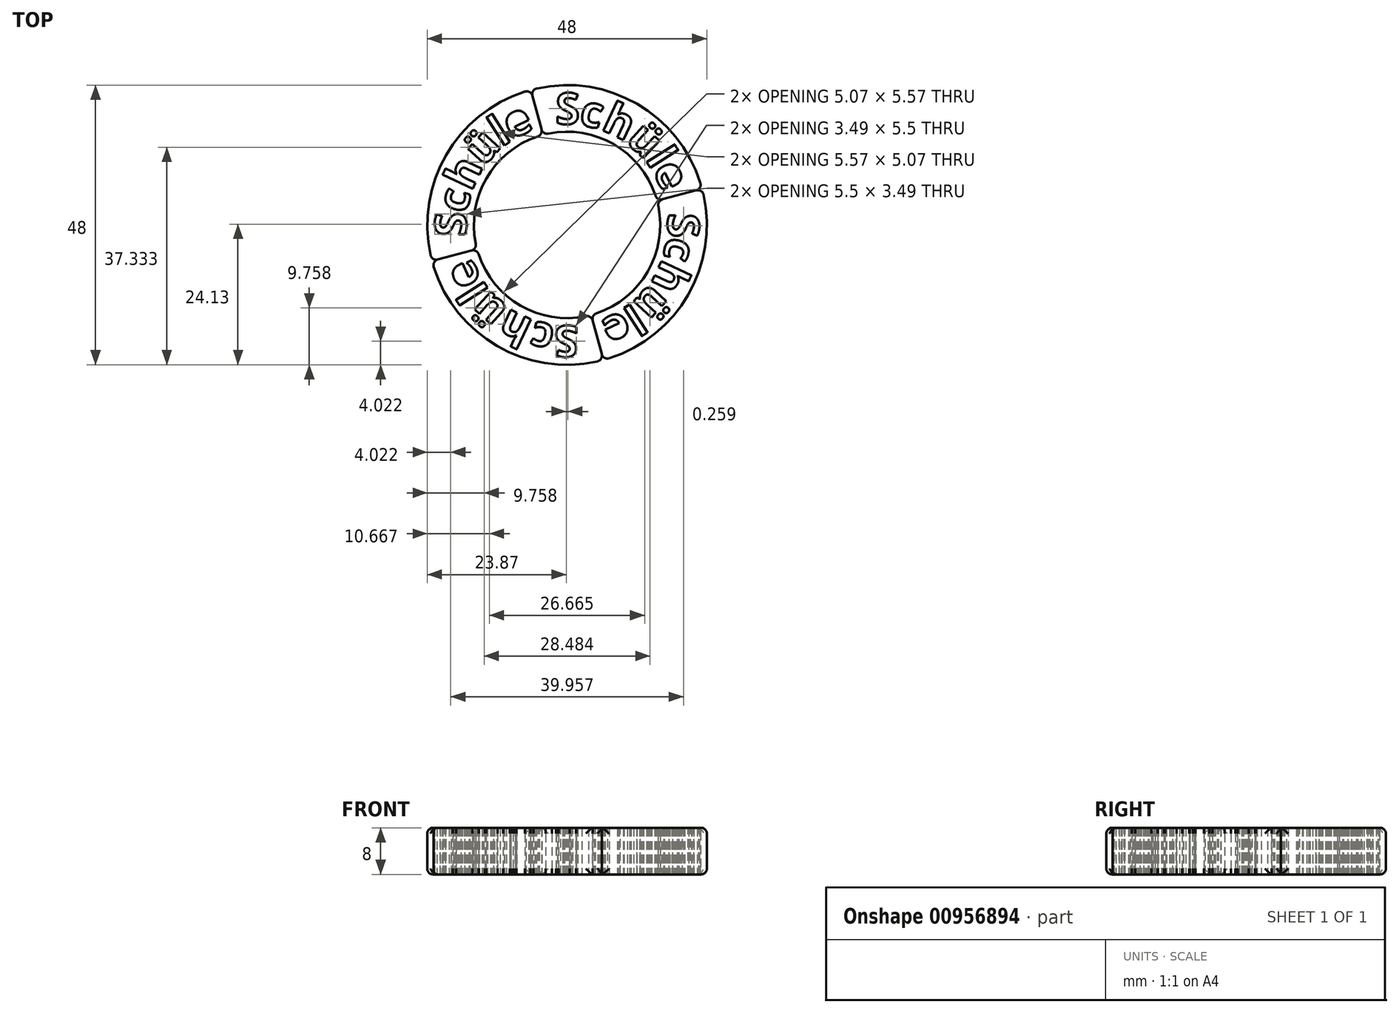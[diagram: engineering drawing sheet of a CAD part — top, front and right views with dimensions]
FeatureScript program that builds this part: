
annotation { "Feature Type Name" : "Feature", "Feature Type Description" : "" }
export const myFeature = defineFeature(function(context is Context, id is Id, definition is map)
    precondition{}
    {
        {
            var Q0;
            Q0=qCreatedBy(makeId("Top.planeOp"),FACE);
            var sketch = newSketch(context, id + "F0", { "sketchPlane" : qUnion([Q0])});
            skArc(sketch, "E0", {"start": v(23.18, 6.21) * mm, "mid": v(12, 20.78) * mm, "end": v(-6.21, 23.18) * mm});
            skArc(sketch, "E1", {"start": v(15.45, 4.14) * mm, "mid": v(8, 13.86) * mm, "end": v(-4.14, 15.45) * mm});
            skText(sketch, "E2", { "text": "c", "fontName": "OpenSans-Bold.ttf"});
            skText(sketch, "E3", { "text": "S", "fontName": "OpenSans-Bold.ttf"});
            skText(sketch, "E4", { "text": "h", "fontName": "OpenSans-Bold.ttf"});
            skText(sketch, "E5", { "text": "ü", "fontName": "OpenSans-Bold.ttf"});
            skText(sketch, "E6", { "text": "l", "fontName": "OpenSans-Bold.ttf"});
            skText(sketch, "E7", { "text": "e", "fontName": "OpenSans-Bold.ttf"});
            skLineSegment(sketch, "E8", {"start": v(15.45, 4.14) * mm, "end": v(23.18, 6.21) * mm});
            skLineSegment(sketch, "E9", {"start": v(-4.14, 15.45) * mm, "end": v(-6.21, 23.18) * mm});
            skLineSegment(sketch, "E10", {"start": v(0, 0) * mm, "end": v(15.45, 4.14) * mm});
            skPoint(sketch, "E11.start.orphan", {"position": v(0, 24) * mm});
            skLineSegment(sketch, "E12", {"start": v(-4.14, 15.45) * mm, "end": v(0, 0) * mm});
            skCircle(sketch, "E13", {"center": v(0, 0) * mm, "radius": 15.95 * mm});
            const initialGuessF0  = {"E2": [0.00188, 0.01736, 0.97037, -0.2416, 0.00533], "E3": [-0.00196, 0.0173, 1, 0, 0.0054], "E4": [0.0057, 0.01644, 0.90447, -0.42653, 0.0054], "E5": [0.0099, 0.01439, 0.73728, -0.6756, 0.0054], "E6": [0.01335, 0.01124, 0.53804, -0.84292, 0.0054], "E7": [0.01463, 0.00952, 0.43051, -0.90259, 0.0054]};
            skSetInitialGuess(sketch, initialGuessF0);
            skSolve(sketch);
        }
        {
            var Q0;
            Q0=makeQuery(id+"F0.imprint","IMPRINT",FACE,{"disambiguationData":[TD([[makeQuery(id+"F0.imprint","IMPRINT",EDGE,{"derivedFrom":sQuery(id+"F0.wireOp",EDGE,"E0")}),1.0]])]});
            var Q1;
            Q1=makeQuery(id+"F0.imprint","IMPRINT",FACE,{"disambiguationData":[TD([[makeQuery(id+"F0.imprint","IMPRINT",EDGE,{"derivedFrom":sQuery(id+"F0.wireOp",EDGE,"E2.sketch_text.stroke-0")}),1.0]])]});
            var Q2;
            {var subQ0=sQuery(id+"F0.wireOp",EDGE,"E10");Q2=makeQuery(id+"F0.imprint","IMPRINT",FACE,{"disambiguationData":[TD([[makeQuery(id+"F0.imprint","IMPRINT",EDGE,{"derivedFrom":subQ0}),1.0]])]});}
            extrude(context, id + "F1", {"entities" : qUnion([Q0, Q1, Q2]), "depth" : 8 * mm, "offsetDistance" : 25 * mm});
        }
        {
            var Q0;
            Q0=makeQuery(id+"F1.opExtrude","SWEPT_BODY",BODY,{"disambiguationData":[OSD([sQuery(id+"F0.wireOp",EDGE,"E0"),sQuery(id+"F0.wireOp",EDGE,"E2.sketch_text.stroke-0"),sQuery(id+"F0.wireOp",EDGE,"E2.sketch_text.stroke-1"),sQuery(id+"F0.wireOp",EDGE,"E2.sketch_text.stroke-2"),sQuery(id+"F0.wireOp",EDGE,"E2.sketch_text.stroke-3"),sQuery(id+"F0.wireOp",EDGE,"E2.sketch_text.stroke-4"),sQuery(id+"F0.wireOp",EDGE,"E2.sketch_text.stroke-5"),sQuery(id+"F0.wireOp",EDGE,"E2.sketch_text.stroke-6"),sQuery(id+"F0.wireOp",EDGE,"E2.sketch_text.stroke-7"),sQuery(id+"F0.wireOp",EDGE,"E2.sketch_text.stroke-8"),sQuery(id+"F0.wireOp",EDGE,"E2.sketch_text.stroke-9"),sQuery(id+"F0.wireOp",EDGE,"E2.sketch_text.stroke-10"),sQuery(id+"F0.wireOp",EDGE,"E2.sketch_text.stroke-11"),sQuery(id+"F0.wireOp",EDGE,"E2.sketch_text.stroke-12"),sQuery(id+"F0.wireOp",EDGE,"E2.sketch_text.stroke-13"),sQuery(id+"F0.wireOp",EDGE,"E3.sketch_text.stroke-0"),sQuery(id+"F0.wireOp",EDGE,"E3.sketch_text.stroke-1"),sQuery(id+"F0.wireOp",EDGE,"E3.sketch_text.stroke-2"),sQuery(id+"F0.wireOp",EDGE,"E3.sketch_text.stroke-3"),sQuery(id+"F0.wireOp",EDGE,"E3.sketch_text.stroke-4"),sQuery(id+"F0.wireOp",EDGE,"E3.sketch_text.stroke-5"),sQuery(id+"F0.wireOp",EDGE,"E3.sketch_text.stroke-6"),sQuery(id+"F0.wireOp",EDGE,"E3.sketch_text.stroke-7"),sQuery(id+"F0.wireOp",EDGE,"E3.sketch_text.stroke-8"),sQuery(id+"F0.wireOp",EDGE,"E3.sketch_text.stroke-9"),sQuery(id+"F0.wireOp",EDGE,"E3.sketch_text.stroke-10"),sQuery(id+"F0.wireOp",EDGE,"E3.sketch_text.stroke-11"),sQuery(id+"F0.wireOp",EDGE,"E3.sketch_text.stroke-12"),sQuery(id+"F0.wireOp",EDGE,"E3.sketch_text.stroke-13"),sQuery(id+"F0.wireOp",EDGE,"E3.sketch_text.stroke-14"),sQuery(id+"F0.wireOp",EDGE,"E3.sketch_text.stroke-15"),sQuery(id+"F0.wireOp",EDGE,"E3.sketch_text.stroke-16"),sQuery(id+"F0.wireOp",EDGE,"E3.sketch_text.stroke-17"),sQuery(id+"F0.wireOp",EDGE,"E3.sketch_text.stroke-18"),sQuery(id+"F0.wireOp",EDGE,"E3.sketch_text.stroke-19"),sQuery(id+"F0.wireOp",EDGE,"E3.sketch_text.stroke-20"),sQuery(id+"F0.wireOp",EDGE,"E3.sketch_text.stroke-21"),sQuery(id+"F0.wireOp",EDGE,"E3.sketch_text.stroke-22"),sQuery(id+"F0.wireOp",EDGE,"E3.sketch_text.stroke-23"),sQuery(id+"F0.wireOp",EDGE,"E3.sketch_text.stroke-24"),sQuery(id+"F0.wireOp",EDGE,"E3.sketch_text.stroke-25"),sQuery(id+"F0.wireOp",EDGE,"E3.sketch_text.stroke-26"),sQuery(id+"F0.wireOp",EDGE,"E3.sketch_text.stroke-27"),sQuery(id+"F0.wireOp",EDGE,"E4.sketch_text.stroke-0"),sQuery(id+"F0.wireOp",EDGE,"E4.sketch_text.stroke-1"),sQuery(id+"F0.wireOp",EDGE,"E4.sketch_text.stroke-2"),sQuery(id+"F0.wireOp",EDGE,"E4.sketch_text.stroke-3"),sQuery(id+"F0.wireOp",EDGE,"E4.sketch_text.stroke-4"),sQuery(id+"F0.wireOp",EDGE,"E4.sketch_text.stroke-5"),sQuery(id+"F0.wireOp",EDGE,"E4.sketch_text.stroke-6"),sQuery(id+"F0.wireOp",EDGE,"E4.sketch_text.stroke-7"),sQuery(id+"F0.wireOp",EDGE,"E4.sketch_text.stroke-8"),sQuery(id+"F0.wireOp",EDGE,"E4.sketch_text.stroke-9"),sQuery(id+"F0.wireOp",EDGE,"E4.sketch_text.stroke-10"),sQuery(id+"F0.wireOp",EDGE,"E4.sketch_text.stroke-11"),sQuery(id+"F0.wireOp",EDGE,"E4.sketch_text.stroke-12"),sQuery(id+"F0.wireOp",EDGE,"E4.sketch_text.stroke-13"),sQuery(id+"F0.wireOp",EDGE,"E4.sketch_text.stroke-14"),sQuery(id+"F0.wireOp",EDGE,"E4.sketch_text.stroke-15"),sQuery(id+"F0.wireOp",EDGE,"E4.sketch_text.stroke-16"),sQuery(id+"F0.wireOp",EDGE,"E5.sketch_text.stroke-0"),sQuery(id+"F0.wireOp",EDGE,"E5.sketch_text.stroke-1"),sQuery(id+"F0.wireOp",EDGE,"E5.sketch_text.stroke-2"),sQuery(id+"F0.wireOp",EDGE,"E5.sketch_text.stroke-3"),sQuery(id+"F0.wireOp",EDGE,"E5.sketch_text.stroke-4"),sQuery(id+"F0.wireOp",EDGE,"E5.sketch_text.stroke-5"),sQuery(id+"F0.wireOp",EDGE,"E5.sketch_text.stroke-6"),sQuery(id+"F0.wireOp",EDGE,"E5.sketch_text.stroke-7"),sQuery(id+"F0.wireOp",EDGE,"E5.sketch_text.stroke-8"),sQuery(id+"F0.wireOp",EDGE,"E5.sketch_text.stroke-9"),sQuery(id+"F0.wireOp",EDGE,"E5.sketch_text.stroke-10"),sQuery(id+"F0.wireOp",EDGE,"E5.sketch_text.stroke-11"),sQuery(id+"F0.wireOp",EDGE,"E5.sketch_text.stroke-12"),sQuery(id+"F0.wireOp",EDGE,"E5.sketch_text.stroke-13"),sQuery(id+"F0.wireOp",EDGE,"E5.sketch_text.stroke-14"),sQuery(id+"F0.wireOp",EDGE,"E5.sketch_text.stroke-15"),sQuery(id+"F0.wireOp",EDGE,"E5.sketch_text.stroke-16"),sQuery(id+"F0.wireOp",EDGE,"E5.sketch_text.stroke-17"),sQuery(id+"F0.wireOp",EDGE,"E5.sketch_text.stroke-18"),sQuery(id+"F0.wireOp",EDGE,"E5.sketch_text.stroke-19"),sQuery(id+"F0.wireOp",EDGE,"E5.sketch_text.stroke-20"),sQuery(id+"F0.wireOp",EDGE,"E5.sketch_text.stroke-21"),sQuery(id+"F0.wireOp",EDGE,"E5.sketch_text.stroke-22"),sQuery(id+"F0.wireOp",EDGE,"E5.sketch_text.stroke-23"),sQuery(id+"F0.wireOp",EDGE,"E5.sketch_text.stroke-24"),sQuery(id+"F0.wireOp",EDGE,"E5.sketch_text.stroke-25"),sQuery(id+"F0.wireOp",EDGE,"E5.sketch_text.stroke-26"),sQuery(id+"F0.wireOp",EDGE,"E5.sketch_text.stroke-27"),sQuery(id+"F0.wireOp",EDGE,"E5.sketch_text.stroke-28"),sQuery(id+"F0.wireOp",EDGE,"E5.sketch_text.stroke-29"),sQuery(id+"F0.wireOp",EDGE,"E5.sketch_text.stroke-30"),sQuery(id+"F0.wireOp",EDGE,"E5.sketch_text.stroke-31"),sQuery(id+"F0.wireOp",EDGE,"E5.sketch_text.stroke-32"),sQuery(id+"F0.wireOp",EDGE,"E6.sketch_text.stroke-0"),sQuery(id+"F0.wireOp",EDGE,"E6.sketch_text.stroke-1"),sQuery(id+"F0.wireOp",EDGE,"E6.sketch_text.stroke-2"),sQuery(id+"F0.wireOp",EDGE,"E6.sketch_text.stroke-3"),sQuery(id+"F0.wireOp",EDGE,"E7.sketch_text.stroke-5"),sQuery(id+"F0.wireOp",EDGE,"E7.sketch_text.stroke-6"),sQuery(id+"F0.wireOp",EDGE,"E7.sketch_text.stroke-7"),sQuery(id+"F0.wireOp",EDGE,"E7.sketch_text.stroke-8"),sQuery(id+"F0.wireOp",EDGE,"E7.sketch_text.stroke-9"),sQuery(id+"F0.wireOp",EDGE,"E7.sketch_text.stroke-10"),sQuery(id+"F0.wireOp",EDGE,"E7.sketch_text.stroke-11"),sQuery(id+"F0.wireOp",EDGE,"E7.sketch_text.stroke-12"),sQuery(id+"F0.wireOp",EDGE,"E7.sketch_text.stroke-13"),sQuery(id+"F0.wireOp",EDGE,"E7.sketch_text.stroke-14"),sQuery(id+"F0.wireOp",EDGE,"E7.sketch_text.stroke-15"),sQuery(id+"F0.wireOp",EDGE,"E7.sketch_text.stroke-16"),sQuery(id+"F0.wireOp",EDGE,"E7.sketch_text.stroke-17"),sQuery(id+"F0.wireOp",EDGE,"E7.sketch_text.stroke-18"),sQuery(id+"F0.wireOp",EDGE,"E7.sketch_text.stroke-19"),sQuery(id+"F0.wireOp",EDGE,"E8"),sQuery(id+"F0.wireOp",EDGE,"E9"),sQuery(id+"F0.wireOp",EDGE,"E10"),sQuery(id+"F0.wireOp",EDGE,"E12")])]});
            var Q1;
            Q1=makeQuery(id+"F1.opExtrude","SWEPT_EDGE",EDGE,{"disambiguationData":[OSD([sQuery(id+"F0.wireOp",EDGE,"E10"),sQuery(id+"F0.wireOp",EDGE,"E12")])]});
            circularPattern(context, id + "F2", {"operationType" : NewBodyOperationType.ADD, "entities" : qUnion([Q0]), "axis" : qUnion([Q1]), "angle" : 360 * degree, "instanceCount" : 4, "equalSpace" : true});
        }
        {
            var Q0;
            {var subQ0=sQuery(id+"F0.wireOp",EDGE,"E12");var subQ1=sQuery(id+"F0.wireOp",EDGE,"E10");var subQ2=makeQuery(id+"F0.imprint","INTERSECT",VERTEX,{"derivedFrom":[subQ1,subQ0]});Q0=makeQuery(id+"F0.imprint","IMPRINT",FACE,{"disambiguationData":[TD([[makeQuery(id+"F0.imprint","IMPRINT",EDGE,{"disambiguationData":[TD([[subQ2,-1.0]])],"derivedFrom":subQ1}),1.0]])]});}
            extrude(context, id + "F3", {"entities" : qUnion([Q0]), "operationType" : NewBodyOperationType.REMOVE, "endBound" : BoundingType.THROUGH_ALL, "depth" : 25 * mm, "offsetDistance" : 25 * mm});
        }
        {
            var Q0;
            {var subQ0=makeQuery(id+"F1.opExtrude","SWEPT_FACE",FACE,{"disambiguationData":[OSD([sQuery(id+"F0.wireOp",EDGE,"E1")])]});Q0=makeQuery(id+"F2.boolean.opBoolean","MERGE",FACE,{"derivedFrom":[subQ0,makeQuery(id+"F2.opPattern","COPY",FACE,{"derivedFrom":subQ0,"instanceName":"1"}),makeQuery(id+"F2.opPattern","COPY",FACE,{"derivedFrom":subQ0,"instanceName":"2"}),makeQuery(id+"F2.opPattern","COPY",FACE,{"derivedFrom":subQ0,"instanceName":"3"})]});}
            var Q1;
            {var subQ0=makeQuery(id+"F1.opExtrude","SWEPT_FACE",FACE,{"disambiguationData":[OSD([sQuery(id+"F0.wireOp",EDGE,"E0")])]});Q1=makeQuery(id+"F2.boolean.opBoolean","MERGE",FACE,{"derivedFrom":[subQ0,makeQuery(id+"F2.opPattern","COPY",FACE,{"derivedFrom":subQ0,"instanceName":"1"}),makeQuery(id+"F2.opPattern","COPY",FACE,{"derivedFrom":subQ0,"instanceName":"2"}),makeQuery(id+"F2.opPattern","COPY",FACE,{"derivedFrom":subQ0,"instanceName":"3"})]});}
            fillet(context, id + "F4", {"entities" : qUnion([Q0, Q1]), "radius" : 1 * mm, "tangentPropagation" : true, "allowEdgeOverflow" : false});
        }
    });
